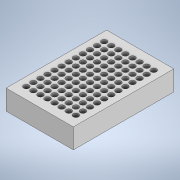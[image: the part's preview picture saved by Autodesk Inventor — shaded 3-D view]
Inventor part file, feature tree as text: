
AUTODESK INVENTOR PART (.ipt)
format: ipt  version: 2020 (Build 240168000, 168)  size: 246,784 bytes
history: native  units: in
note: dims shown in document units (in); Inventor stores cm internally (conversion verified against a paired STEP export)
features: sketch x2, extrude x1, hole x1, pattern_linear x1
ambient origin geometry x8: Origin, YZ Plane, XZ Plane, XY Plane, X Axis, Y Axis, Z Axis, Center Point
bodies: Solid1 (feature_tree)
feature tree (5):
  extrude  "Extrusion1"  Depth=5.03in
  hole  "Hole1"  [1 undecoded]
  pattern_linear  "Rectangular Pattern1"  Spacing1=0.5661in  [1 undecoded]
  sketch  "Sketch1"  dims[d0=3.365in d1=5.03in]
  sketch  "Sketch2"  dims[d2=1.0in d3=0.0in d4=0.4425in d5=0.5661in d6=0.2756in d7=0.2756in d8=0.75in d9=0.37in d10=0.25in d11=90.0deg d12=0.75in d13=0.0in d14=3.1496in d16=0.3543in d17=4.7244in d19=0.3543in]
note: 2 required parameter values undecoded (feature->parameter linkage not recoverable at this tier; creation-order binding heuristic only, values carry confidence <= 0.55)
